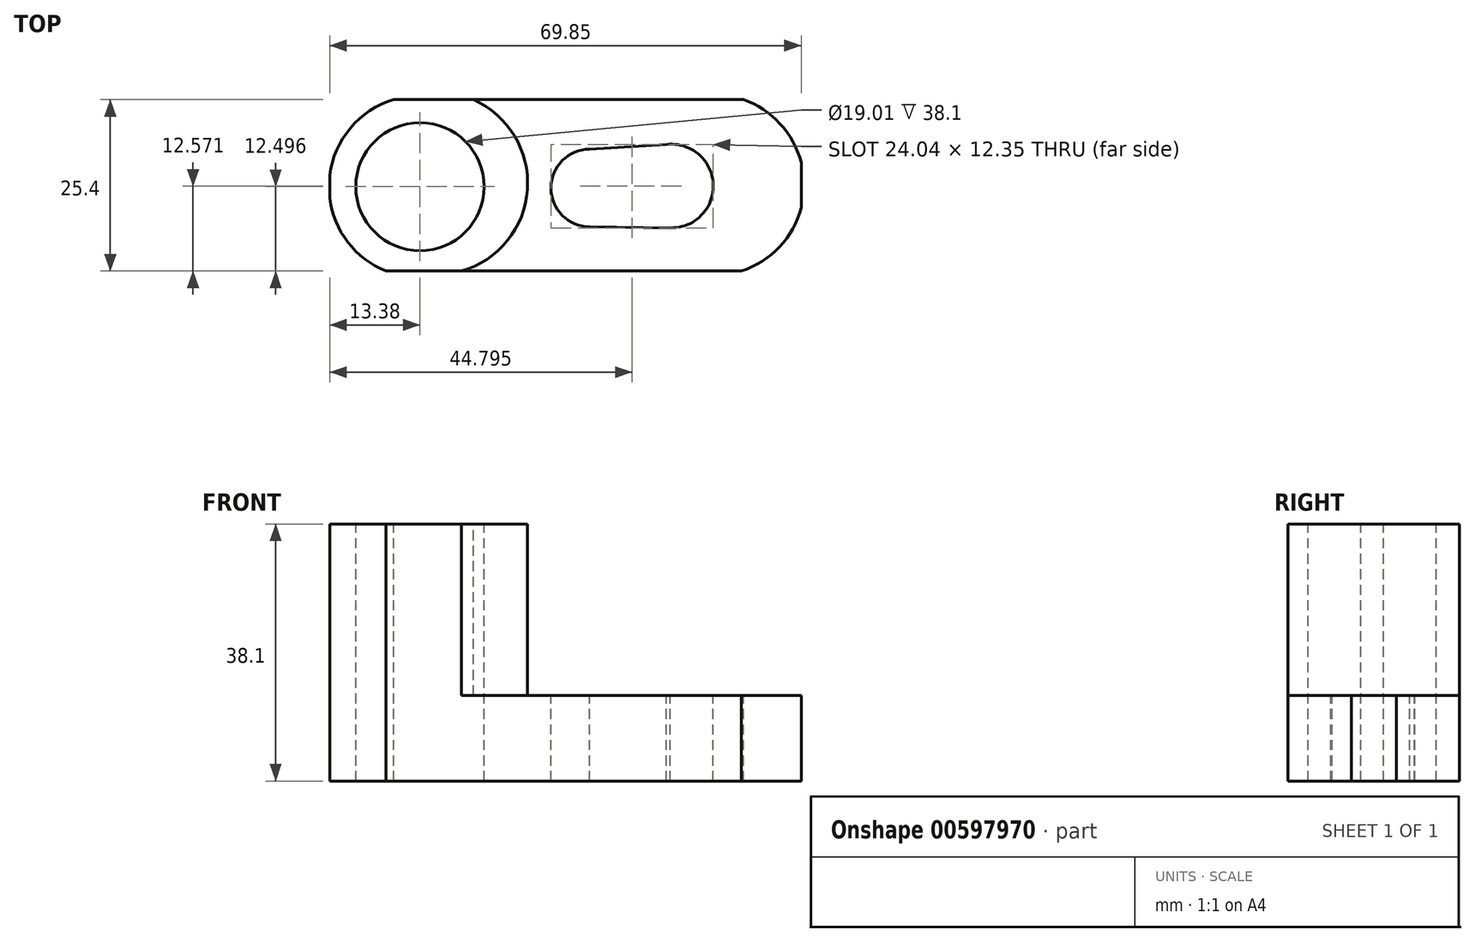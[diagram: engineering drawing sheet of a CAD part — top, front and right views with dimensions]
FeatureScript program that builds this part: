
annotation { "Feature Type Name" : "Feature", "Feature Type Description" : "" }
export const myFeature = defineFeature(function(context is Context, id is Id, definition is map)
    precondition{}
    {
        {
            var Q0;
            Q0=qCreatedBy(makeId("Front.planeOp"),FACE);
            var sketch = newSketch(context, id + "F0", { "sketchPlane" : qUnion([Q0])});
            skLineSegment(sketch, "E0", {"start": v(-42.13, 38.1) * mm, "end": v(-42.13, 0) * mm});
            skLineSegment(sketch, "E1", {"start": v(-42.13, 0) * mm, "end": v(27.72, 0) * mm});
            skLineSegment(sketch, "E2", {"start": v(27.72, 0) * mm, "end": v(27.72, 38.1) * mm});
            skLineSegment(sketch, "E3", {"start": v(-42.13, 38.1) * mm, "end": v(27.72, 38.1) * mm});
            skSolve(sketch);
        }
        {
            var Q0;
            Q0=makeQuery(id+"F0.imprint","IMPRINT",FACE,{"disambiguationData":[TD([[makeQuery(id+"F0.imprint","IMPRINT",EDGE,{"derivedFrom":sQuery(id+"F0.wireOp",EDGE,"E0")}),1.0]])]});
            extrude(context, id + "F1", {"entities" : qUnion([Q0]), "depth" : 25.4 * mm, "offsetDistance" : 25.4 * mm});
        }
        {
            var Q0;
            Q0=makeQuery(id+"F1.opExtrude","SWEPT_FACE",FACE,{"disambiguationData":[OSD([sQuery(id+"F0.wireOp",EDGE,"E3")])]});
            var sketch = newSketch(context, id + "F2", { "sketchPlane" : qUnion([Q0])});
            skArc(sketch, "E4", {"start": v(-32.67, 0) * mm, "mid": v(-42.22, -12.3) * mm, "end": v(-33.82, -25.4) * mm});
            skArc(sketch, "E5", {"start": v(18.85, -25.4) * mm, "mid": v(28.14, -12.8) * mm, "end": v(19.14, 0) * mm});
            skSolve(sketch);
        }
        {
            var Q0;
            Q0 = qSketchRegion(id + "F2", true);
            var Q1;
            {var subQ0=sQuery(id+"F2.wireOp",EDGE,"E4");var subQ1=sQuery(id+"F0.wireOp",EDGE,"E3");var subQ2=makeQuery(id+"F1.opExtrude","CAP_EDGE",EDGE,{"disambiguationData":[OSD([subQ1])],"isStart":true});var subQ3=makeQuery(id+"F2.imprint","INTERSECT",VERTEX,{"derivedFrom":[subQ2,subQ0]});Q1=makeQuery(id+"F2.imprint","IMPRINT",FACE,{"disambiguationData":[TD([[makeQuery(id+"F2.imprint","IMPRINT",EDGE,{"disambiguationData":[TD([[subQ3,-1.0]])],"derivedFrom":subQ0}),-1.0]])]});}
            var Q2;
            {var subQ0=sQuery(id+"F2.wireOp",EDGE,"E4");var subQ1=sQuery(id+"F0.wireOp",EDGE,"E3");var subQ2=makeQuery(id+"F1.opExtrude","CAP_EDGE",EDGE,{"disambiguationData":[OSD([subQ1])],"isStart":false});var subQ3=makeQuery(id+"F2.imprint","INTERSECT",VERTEX,{"derivedFrom":[subQ2,subQ0]});Q2=makeQuery(id+"F2.imprint","IMPRINT",FACE,{"disambiguationData":[TD([[makeQuery(id+"F2.imprint","IMPRINT",EDGE,{"disambiguationData":[TD([[subQ3,1.0]])],"derivedFrom":subQ0}),-1.0]])]});}
            var Q3;
            {var subQ0=sQuery(id+"F2.wireOp",EDGE,"E5");var subQ1=sQuery(id+"F0.wireOp",EDGE,"E3");var subQ2=makeQuery(id+"F1.opExtrude","CAP_EDGE",EDGE,{"disambiguationData":[OSD([subQ1])],"isStart":false});var subQ3=makeQuery(id+"F2.imprint","INTERSECT",VERTEX,{"derivedFrom":[subQ2,subQ0]});Q3=makeQuery(id+"F2.imprint","IMPRINT",FACE,{"disambiguationData":[TD([[makeQuery(id+"F2.imprint","IMPRINT",EDGE,{"disambiguationData":[TD([[subQ3,-1.0]])],"derivedFrom":subQ0}),-1.0]])]});}
            var Q4;
            {var subQ0=sQuery(id+"F2.wireOp",EDGE,"E5");var subQ1=sQuery(id+"F0.wireOp",EDGE,"E3");var subQ2=makeQuery(id+"F1.opExtrude","CAP_EDGE",EDGE,{"disambiguationData":[OSD([subQ1])],"isStart":true});var subQ3=makeQuery(id+"F2.imprint","INTERSECT",VERTEX,{"derivedFrom":[subQ2,subQ0]});Q4=makeQuery(id+"F2.imprint","IMPRINT",FACE,{"disambiguationData":[TD([[makeQuery(id+"F2.imprint","IMPRINT",EDGE,{"disambiguationData":[TD([[subQ3,1.0]])],"derivedFrom":subQ0}),-1.0]])]});}
            extrude(context, id + "F3", {"entities" : qUnion([Q0, Q1, Q2, Q3, Q4]), "operationType" : NewBodyOperationType.REMOVE, "endBound" : BoundingType.THROUGH_ALL, "oppositeDirection" : true, "depth" : 25.4 * mm, "offsetDistance" : 25.4 * mm});
        }
        {
            var Q0;
            Q0=makeQuery(id+"F1.opExtrude","SWEPT_FACE",FACE,{"disambiguationData":[OSD([sQuery(id+"F0.wireOp",EDGE,"E3")])]});
            var sketch = newSketch(context, id + "F4", { "sketchPlane" : qUnion([Q0])});
            skArc(sketch, "E6", {"start": v(-22.6, -25.4) * mm, "mid": v(-12.84, -13.3) * mm, "end": v(-20.87, 0) * mm});
            skSolve(sketch);
        }
        {
            var Q0;
            {var subQ7=sQuery(id+"F4.wireOp",EDGE,"E6");Q0=makeQuery(id+"F4.imprint","IMPRINT",FACE,{"disambiguationData":[TD([[makeQuery(id+"F4.imprint","IMPRINT",EDGE,{"derivedFrom":subQ7}),-1.0]])]});}
            extrude(context, id + "F5", {"entities" : qUnion([Q0]), "operationType" : NewBodyOperationType.REMOVE, "oppositeDirection" : true, "depth" : 25.4 * mm, "offsetDistance" : 25.4 * mm});
        }
        {
            var Q0;
            Q0=makeQuery(id+"F1.opExtrude","SWEPT_FACE",FACE,{"disambiguationData":[OSD([sQuery(id+"F0.wireOp",EDGE,"E3")])]});
            var sketch = newSketch(context, id + "F6", { "sketchPlane" : qUnion([Q0])});
            skCircle(sketch, "E7", {"center": v(-28.75, -12.9) * mm, "radius": 9.5 * mm});
            skSolve(sketch);
        }
        {
            var Q0;
            Q0=makeQuery(id+"F6.imprint","IMPRINT",FACE,{"disambiguationData":[TD([[makeQuery(id+"F6.imprint","IMPRINT",EDGE,{"derivedFrom":sQuery(id+"F6.wireOp",EDGE,"E7")}),1.0]])]});
            extrude(context, id + "F7", {"entities" : qUnion([Q0]), "operationType" : NewBodyOperationType.REMOVE, "endBound" : BoundingType.THROUGH_ALL, "oppositeDirection" : true, "depth" : 25.4 * mm, "offsetDistance" : 25.4 * mm});
        }
        {
            var Q0;
            Q0=makeQuery(id+"F5.boolean.opBoolean","COPY",FACE,{"derivedFrom":makeQuery(id+"F5.opExtrude","CAP_FACE",FACE,{"disambiguationData":[OSD([sQuery(id+"F0.wireOp",EDGE,"E2"),sQuery(id+"F0.wireOp",EDGE,"E3"),sQuery(id+"F2.wireOp",EDGE,"E5"),sQuery(id+"F4.wireOp",EDGE,"E6")])],"isStart":false})});
            var sketch = newSketch(context, id + "F8", { "sketchPlane" : qUnion([Q0])});
            skCircle(sketch, "E8", {"center": v(-3.6, -13.1) * mm, "radius": 5.76 * mm});
            skCircle(sketch, "E9", {"center": v(8.5, -12.8) * mm, "radius": 6.2 * mm});
            skLineSegment(sketch, "E10", {"start": v(-3.6, -7.34) * mm, "end": v(8.5, -6.6) * mm});
            skLineSegment(sketch, "E11", {"start": v(-3.6, -18.85) * mm, "end": v(8.5, -19) * mm});
            skSolve(sketch);
        }
        {
            var Q0;
            Q0 = qSketchRegion(id + "F8", true);
            extrude(context, id + "F9", {"entities" : qUnion([Q0]), "operationType" : NewBodyOperationType.REMOVE, "endBound" : BoundingType.THROUGH_ALL, "oppositeDirection" : true, "depth" : 25.4 * mm, "offsetDistance" : 25.4 * mm});
        }
    });
